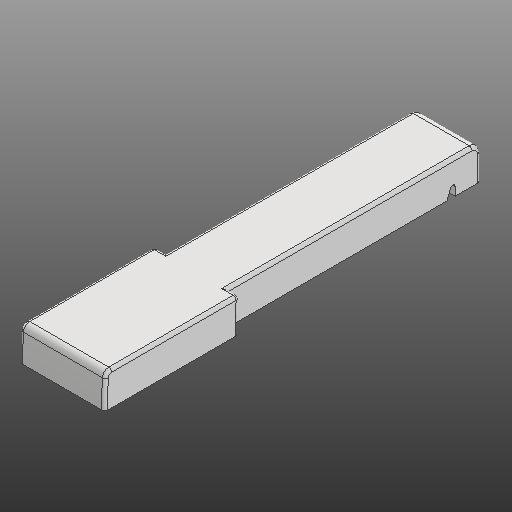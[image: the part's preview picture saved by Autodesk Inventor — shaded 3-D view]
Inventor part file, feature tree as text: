
AUTODESK INVENTOR PART (.ipt)
format: ipt  version: 2020 (Build 240168000, 168)  size: 293,376 bytes
history: native  units: in
note: dims shown in document units (in); Inventor stores cm internally (conversion verified against a paired STEP export)
features: extrude x4, other x3, fillet x2
ambient origin geometry x8: Origin, YZ Plane, XZ Plane, XY Plane, X Axis, Y Axis, Z Axis, Center Point
bodies: Solid1 (feature_tree)
feature tree (9):
  other  "Slot Start Plane"
  other  "Key Profile"
  extrude  "Upper"  TaperAngle=0.0deg  [1 undecoded]
  extrude  "Lower"  TaperAngle=0.0deg  [1 undecoded]
  extrude  "Protrusion Cutout"  Depth=0.0591in
  fillet  "Front Fillet"  Radius=0.1374in
  extrude  "Slot"  [1 undecoded]
  fillet  "Edge Softening"  Radius=0.0787in
  other  "Slot Sketch"
note: 3 required parameter values undecoded (feature->parameter linkage not recoverable at this tier; creation-order binding heuristic only, values carry confidence <= 0.55)
